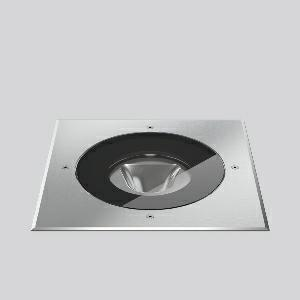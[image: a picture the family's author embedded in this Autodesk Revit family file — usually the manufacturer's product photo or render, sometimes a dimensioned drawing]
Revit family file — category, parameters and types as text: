
# Revit family: terra_edelstahl_245_641289_000_171d
name_source: partatom
category: Lighting Fixtures
units: mm (PartAtom-declared; Revit-internal decimal feet)

## family parameters
Cut with Voids When Loaded = No
Host = Face
Light Source = No
Part Type = Normal
Room Calculation Point = No
Round Connector Dimension = Use Diameter
Shared = No

## types (1)
- TERRA EDELSTAHL 245 (1 x LED Modul 830, 2150 lm, 3000)
    Apparent Load = 28 VA
    CIE Flux Codes = 0 0 0 0 100
    Color Rendering = 80
    Color Temperature = 3000
    Default Elevation = 1800 mm
    Description = Series: TERRA EDELSTAHL 245
In-ground luminaire for pedestrian areas. Housing made of corrosion-resistant die-cast aluminium, powder-coated. Marine grade stainless steel square shaped cover and screws. Flush mounted toughened glass. High-performance LED freeform mirror optics with asymmetrical light distribution. Integral flexible power cord H07-RN8F. Use of in-ground support is necessary, please order chosen version for your application separately. 
Colour: stainless steel
Length: 245 mm
Width: 245 mm
Height: 2 mm
Lamp: LED
System power: 28 W
Rated luminous flux: 2150 lm
Luminous efficiency: 77 lm/W
Control gear: Converter not necessary
Protection class: I
Type of protection: IP 68
    Height = 0 mm  [stored 0 ft]
    Lamp = 1 x LED Modul 830
    Lamp Light Flux = 2150 lm
    Lamp count = 1
    Length = 245 mm
    Lifetime = 50000 h
    Luminous efficacy = 77 lm/W
    Manufacturer = RZB
    ModVariant = No
    Model = 641289.000
    Mounting Place = Floor
    Mounting Type = Recessed
    Number of Poles = 1
    OnlyDefault = Yes
    Power Factor = 1
    Product Name = TERRA EDELSTAHL 245
    Product group = Ground recessed luminaire
    ProductGroupID = 3381
    Protection Class = Protection class I
    Protection Degree = IP 68
    RLX_Detail_Level = 1
    RLX_Emergency_Light_Flux = 0 lm
    RLX_Emergency_Type = 0
    RLX_Emergency_Type_DB = No
    RlxData = <blob elided: 52353 chars, md5=d9c641e6>
    Socket = socket
    Standby Power = 0 W
    System Light Flux = 2150 lm
    System Power = 28 W
    Type Comments = ALEA SPOT
    Type Image = 641289.000.jpg
    URL = http://relux.com
    VarID = ---
    Voltage = 230 V
    Voltage Range = 220-240 V
    Weight = 0.00 kg
    Width = 245 mm

note: [stored X ft] marks values corroborated as IEEE doubles in the binary element streams (Revit-internal decimal feet)

## geometry (parser evidence)
native form markers: Blend x4, Sweep x12
no freeform markers — native parametric forms only
